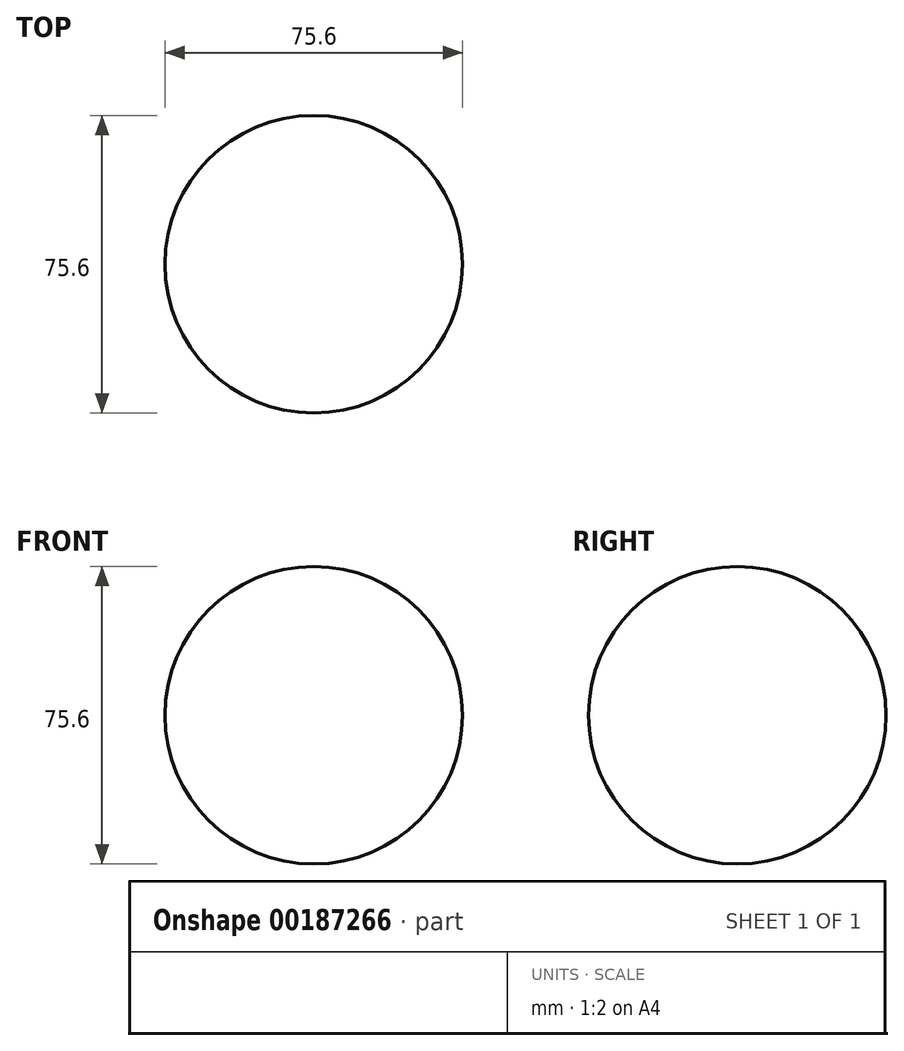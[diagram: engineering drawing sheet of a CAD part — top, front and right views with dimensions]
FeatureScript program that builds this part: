
annotation { "Feature Type Name" : "Feature", "Feature Type Description" : "" }
export const myFeature = defineFeature(function(context is Context, id is Id, definition is map)
    precondition{}
    {
        {
            var Q0;
            Q0=qCreatedBy(makeId("Top.planeOp"),FACE);
            var sketch = newSketch(context, id + "F0", { "sketchPlane" : qUnion([Q0])});
            skLineSegment(sketch, "E0", {"start": v(0, 37.8) * mm, "end": v(0, -37.8) * mm});
            skArc(sketch, "E1", {"start": v(0, 37.8) * mm, "mid": v(37.8, 0) * mm, "end": v(0, -37.8) * mm});
            skSolve(sketch);
        }
        {
            var Q0;
            Q0 = qSketchRegion(id + "F0", true);
            var Q1;
            Q1=sQuery(id+"F0.wireOp",EDGE,"E0");
            revolve(context, id + "F1", {"entities" : qUnion([Q0]), "axis" : qUnion([Q1]), "revolveType" : RevolveType.FULL});
        }
    });
